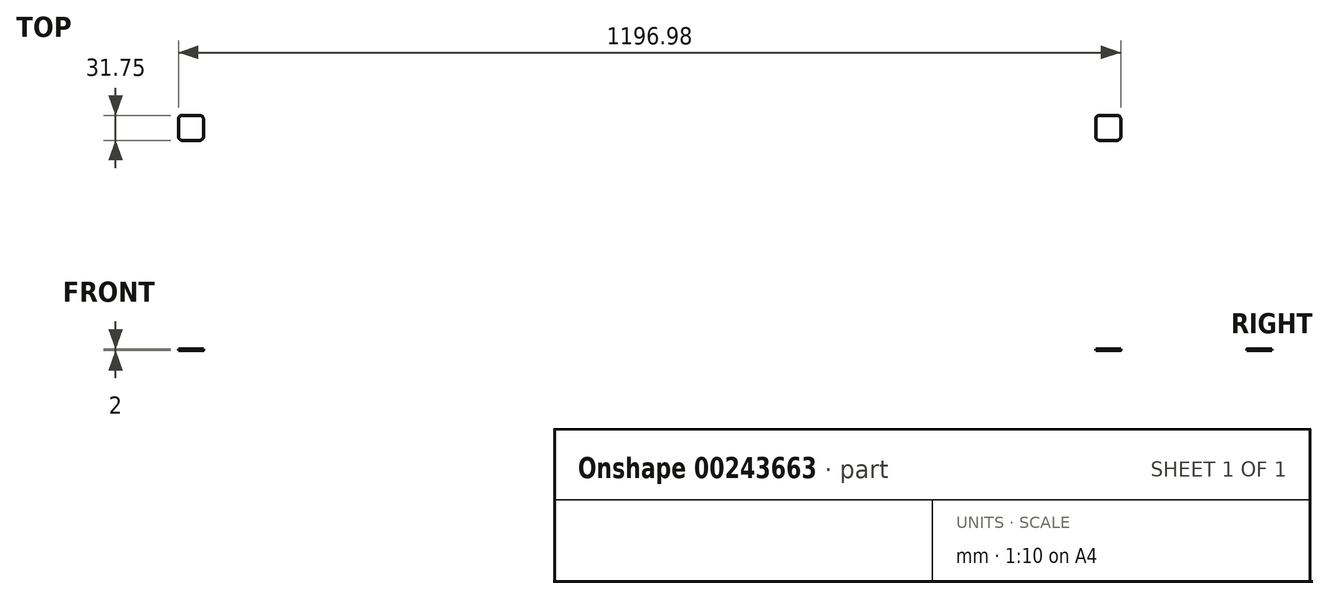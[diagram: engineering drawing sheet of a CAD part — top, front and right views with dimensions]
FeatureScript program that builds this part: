
annotation { "Feature Type Name" : "Feature", "Feature Type Description" : "" }
export const myFeature = defineFeature(function(context is Context, id is Id, definition is map)
    precondition{}
    {
        {
            var Q0;
            Q0=qCreatedBy(makeId("Top.planeOp"),FACE);
            var sketch = newSketch(context, id + "F0", { "sketchPlane" : qUnion([Q0])});
            skLineSegment(sketch, "E0.bottom", {"start": v(-598.49, -220.66) * mm, "end": v(598.49, -220.66) * mm});
            skLineSegment(sketch, "E0.top", {"start": v(-598.49, 220.66) * mm, "end": v(598.49, 220.66) * mm});
            skLineSegment(sketch, "E0.left", {"start": v(-598.49, -220.66) * mm, "end": v(-598.49, 220.66) * mm});
            skLineSegment(sketch, "E0.right", {"start": v(598.49, -220.66) * mm, "end": v(598.49, 220.66) * mm});
            skPoint(sketch, "E0.middle", {"position": v(0, 0) * mm});
            skLineSegment(sketch, "E1.bottom", {"start": v(-598.49, 220.66) * mm, "end": v(-566.74, 220.66) * mm});
            skLineSegment(sketch, "E1.top", {"start": v(-598.49, 188.91) * mm, "end": v(-566.74, 188.91) * mm});
            skLineSegment(sketch, "E1.left", {"start": v(-598.49, 220.66) * mm, "end": v(-598.49, 188.91) * mm});
            skLineSegment(sketch, "E1.right", {"start": v(-566.74, 220.66) * mm, "end": v(-566.74, 188.91) * mm});
            skLineSegment(sketch, "E2.bottom", {"start": v(-598.49, -220.66) * mm, "end": v(-566.74, -220.66) * mm});
            skLineSegment(sketch, "E2.top", {"start": v(-598.49, -188.91) * mm, "end": v(-566.74, -188.91) * mm});
            skLineSegment(sketch, "E2.left", {"start": v(-598.49, -220.66) * mm, "end": v(-598.49, -188.91) * mm});
            skLineSegment(sketch, "E2.right", {"start": v(-566.74, -220.66) * mm, "end": v(-566.74, -188.91) * mm});
            skLineSegment(sketch, "E3.bottom", {"start": v(598.49, 220.66) * mm, "end": v(566.74, 220.66) * mm});
            skLineSegment(sketch, "E3.top", {"start": v(598.49, 188.91) * mm, "end": v(566.74, 188.91) * mm});
            skLineSegment(sketch, "E3.left", {"start": v(598.49, 220.66) * mm, "end": v(598.49, 188.91) * mm});
            skLineSegment(sketch, "E3.right", {"start": v(566.74, 220.66) * mm, "end": v(566.74, 188.91) * mm});
            skLineSegment(sketch, "E4.bottom", {"start": v(598.49, -220.66) * mm, "end": v(566.74, -220.66) * mm});
            skLineSegment(sketch, "E4.top", {"start": v(598.49, -188.91) * mm, "end": v(566.74, -188.91) * mm});
            skLineSegment(sketch, "E4.left", {"start": v(598.49, -220.66) * mm, "end": v(598.49, -188.91) * mm});
            skLineSegment(sketch, "E4.right", {"start": v(566.74, -220.66) * mm, "end": v(566.74, -188.91) * mm});
            skSolve(sketch);
        }
        {
            var Q0;
            Q0=makeQuery(id+"F0.imprint","IMPRINT",FACE,{"disambiguationData":[TD([[makeQuery(id+"F0.imprint","IMPRINT",EDGE,{"derivedFrom":sQuery(id+"F0.wireOp",EDGE,"E0.bottom")}),1.0]])]});
            extrude(context, id + "F1", {"entities" : qUnion([Q0]), "endBound" : BoundingType.SYMMETRIC, "depth" : 2 * mm});
        }
        {
            var Q0;
            Q0=makeQuery(id+"F1.opExtrude","SWEPT_EDGE",EDGE,{"disambiguationData":[OSD([sQuery(id+"F0.wireOp",EDGE,"E0.left"),sQuery(id+"F0.wireOp",EDGE,"E2.top"),sQuery(id+"F0.wireOp",EDGE,"E2.left")])]});
            var Q1;
            Q1=makeQuery(id+"F1.opExtrude","SWEPT_EDGE",EDGE,{"disambiguationData":[OSD([sQuery(id+"F0.wireOp",EDGE,"E2.top"),sQuery(id+"F0.wireOp",EDGE,"E2.right")])]});
            var Q2;
            Q2=makeQuery(id+"F1.opExtrude","SWEPT_EDGE",EDGE,{"disambiguationData":[OSD([sQuery(id+"F0.wireOp",EDGE,"E0.bottom"),sQuery(id+"F0.wireOp",EDGE,"E2.bottom"),sQuery(id+"F0.wireOp",EDGE,"E2.right")])]});
            var Q3;
            Q3=makeQuery(id+"F1.opExtrude","SWEPT_EDGE",EDGE,{"disambiguationData":[OSD([sQuery(id+"F0.wireOp",EDGE,"E0.top"),sQuery(id+"F0.wireOp",EDGE,"E1.bottom"),sQuery(id+"F0.wireOp",EDGE,"E1.right")])]});
            var Q4;
            Q4=makeQuery(id+"F1.opExtrude","SWEPT_EDGE",EDGE,{"disambiguationData":[OSD([sQuery(id+"F0.wireOp",EDGE,"E1.top"),sQuery(id+"F0.wireOp",EDGE,"E1.right")])]});
            var Q5;
            Q5=makeQuery(id+"F1.opExtrude","SWEPT_EDGE",EDGE,{"disambiguationData":[OSD([sQuery(id+"F0.wireOp",EDGE,"E0.left"),sQuery(id+"F0.wireOp",EDGE,"E1.top"),sQuery(id+"F0.wireOp",EDGE,"E1.left")])]});
            var Q6;
            Q6=makeQuery(id+"F1.opExtrude","SWEPT_EDGE",EDGE,{"disambiguationData":[OSD([sQuery(id+"F0.wireOp",EDGE,"E0.top"),sQuery(id+"F0.wireOp",EDGE,"E3.bottom"),sQuery(id+"F0.wireOp",EDGE,"E3.right")])]});
            var Q7;
            Q7=makeQuery(id+"F1.opExtrude","SWEPT_EDGE",EDGE,{"disambiguationData":[OSD([sQuery(id+"F0.wireOp",EDGE,"E3.top"),sQuery(id+"F0.wireOp",EDGE,"E3.right")])]});
            var Q8;
            Q8=makeQuery(id+"F1.opExtrude","SWEPT_EDGE",EDGE,{"disambiguationData":[OSD([sQuery(id+"F0.wireOp",EDGE,"E0.right"),sQuery(id+"F0.wireOp",EDGE,"E3.top"),sQuery(id+"F0.wireOp",EDGE,"E3.left")])]});
            var Q9;
            Q9=makeQuery(id+"F1.opExtrude","SWEPT_EDGE",EDGE,{"disambiguationData":[OSD([sQuery(id+"F0.wireOp",EDGE,"E0.right"),sQuery(id+"F0.wireOp",EDGE,"E4.top"),sQuery(id+"F0.wireOp",EDGE,"E4.left")])]});
            var Q10;
            Q10=makeQuery(id+"F1.opExtrude","SWEPT_EDGE",EDGE,{"disambiguationData":[OSD([sQuery(id+"F0.wireOp",EDGE,"E4.top"),sQuery(id+"F0.wireOp",EDGE,"E4.right")])]});
            var Q11;
            Q11=makeQuery(id+"F1.opExtrude","SWEPT_EDGE",EDGE,{"disambiguationData":[OSD([sQuery(id+"F0.wireOp",EDGE,"E0.bottom"),sQuery(id+"F0.wireOp",EDGE,"E4.bottom"),sQuery(id+"F0.wireOp",EDGE,"E4.right")])]});
            fillet(context, id + "F2", {"entities" : qUnion([Q0, Q1, Q2, Q3, Q4, Q5, Q6, Q7, Q8, Q9, Q10, Q11]), "radius" : 4.76 * mm, "tangentPropagation" : true, "allowEdgeOverflow" : false});
        }
    });
